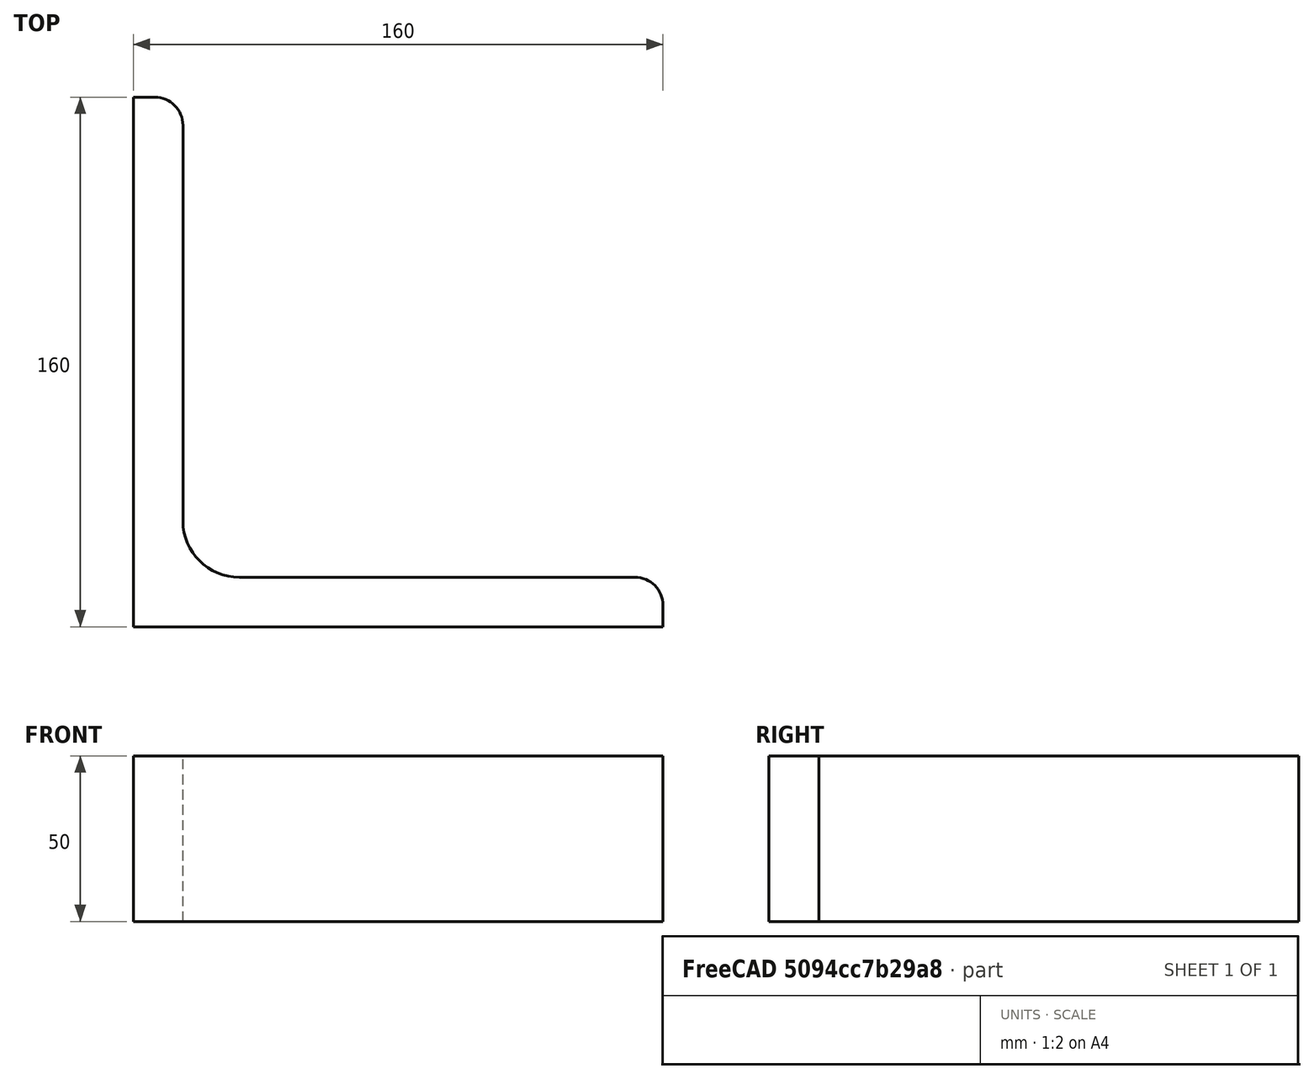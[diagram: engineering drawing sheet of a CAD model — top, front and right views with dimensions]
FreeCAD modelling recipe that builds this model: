
FCSTD DOCUMENT  (FreeCAD 0.15R4671 (Git))
Label: Angle Bar L160x160x15 EN10056 S235JR
License: All rights reserved
LicenseURL: http://en.wikipedia.org/wiki/All_rights_reserved
objects: Sketcher::SketchObject×1, Part::Extrusion×1
note: 2 computed .brp shape members not serialized (recipe doc carries the construction recipe); baked Part::Feature solids carry a one-line shape summary decoded from their .brp

FEATURE [Sketcher::SketchObject] Sketch
  sketch-geometry (9):
    g0: LineSegment StartX=0 StartY=0 StartZ=0 EndX=160 EndY=0 EndZ=0
    g1: LineSegment StartX=160 StartY=0 StartZ=0 EndX=160 EndY=6.5 EndZ=0
    g2: LineSegment StartX=151.5 StartY=15 StartZ=0 EndX=32 EndY=15 EndZ=0
    g3: LineSegment StartX=0 StartY=0 StartZ=0 EndX=0 EndY=160 EndZ=0
    g4: LineSegment StartX=0 StartY=160 StartZ=0 EndX=6.5 EndY=160 EndZ=0
    g5: LineSegment StartX=15 StartY=151.5 StartZ=0 EndX=15 EndY=32 EndZ=0
    g6: ArcOfCircle CenterX=32 CenterY=32 CenterZ=0 NormalX=0 NormalY=0 NormalZ=1 Radius=17 StartAngle=3.14159 EndAngle=4.71239
    g7: ArcOfCircle CenterX=6.5 CenterY=151.5 CenterZ=0 NormalX=0 NormalY=0 NormalZ=1 Radius=8.5 StartAngle=0 EndAngle=1.5708
    g8: ArcOfCircle CenterX=151.5 CenterY=6.5 CenterZ=0 NormalX=0 NormalY=0 NormalZ=1 Radius=8.5 StartAngle=0 EndAngle=1.5708
  constraints (23):
    c: Coincident(g0,g-1)
    c: Horizontal(g0)
    c: Coincident(g1,g0)
    c: Vertical(g1)
    c: Horizontal(g2)
    c: Coincident(g3,g-1)
    c: Vertical(g3)
    c: Coincident(g4,g3)
    c: Horizontal(g4)
    c: Vertical(g5)
    c: Tangent(g5,g6) = -1.5708
    c: Tangent(g2,g6) = 1.5708
    c: Tangent(g4,g7) = 1.5708
    c: Tangent(g5,g7) = 1.5708
    c: Tangent(g2,g8) = -1.5708
    c: Tangent(g1,g8) = -1.5708
    c: DistanceX(g0) = 160
    c: DistanceY(g3) = 160
    c: DistanceY(g0,g2) = 15
    c: DistanceX(g3,g5) = 15
    c: Radius(g6) = 17
    c: Radius(g8) = 8.5
    c: Radius(g7) = 8.5
FEATURE [Part::Extrusion] Extrude  label="Angle Bar L160x160x15 EN10056 S235JR"
  Base = -> Sketch
  Dir = (0,0,50)
  Solid = true
